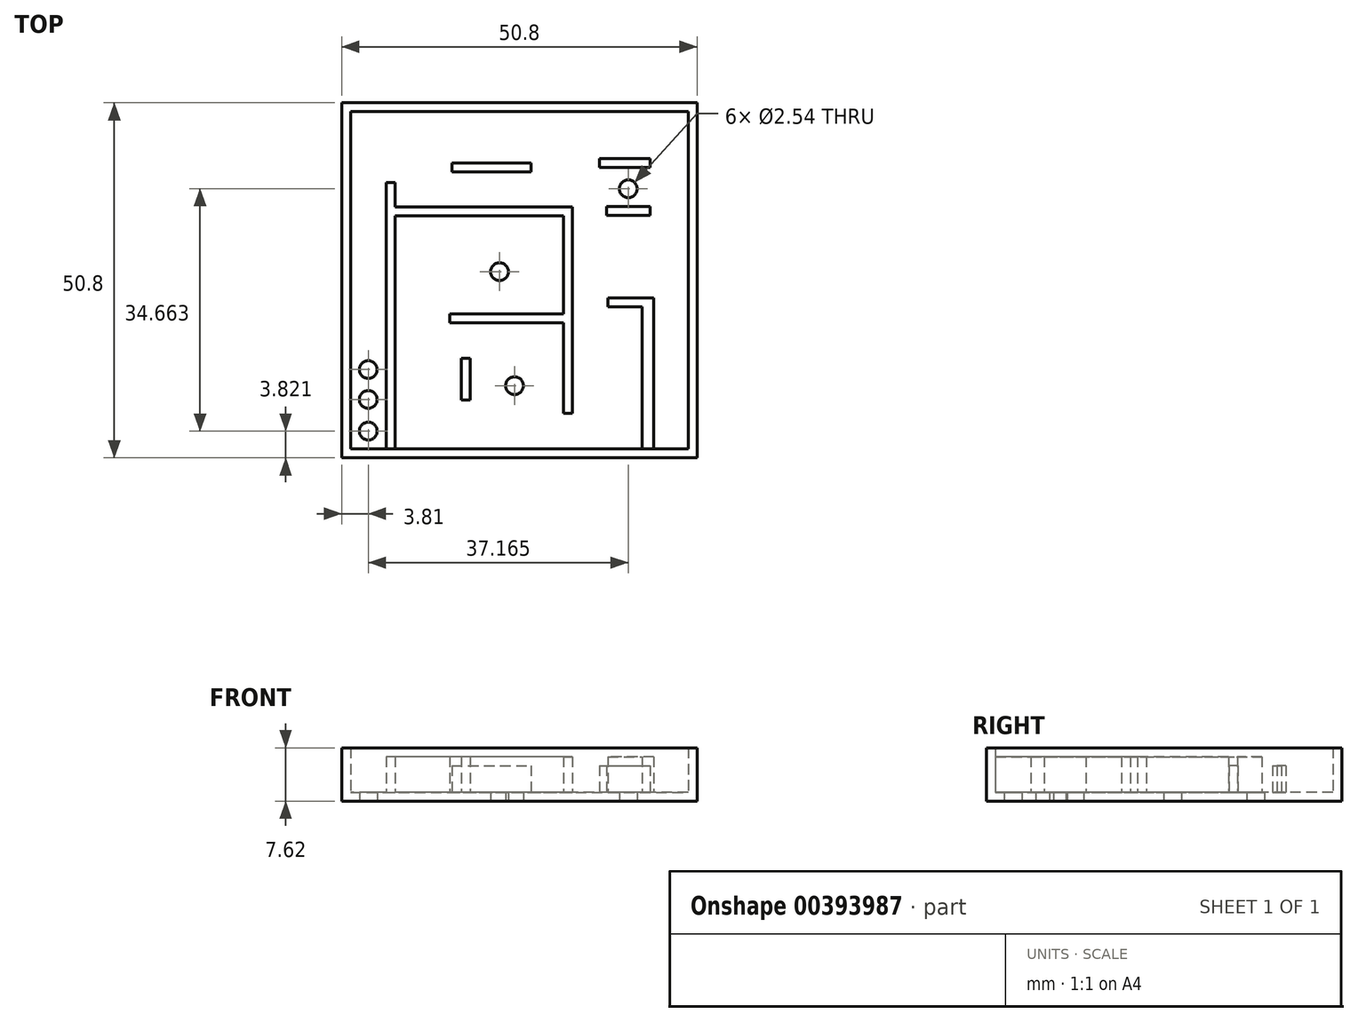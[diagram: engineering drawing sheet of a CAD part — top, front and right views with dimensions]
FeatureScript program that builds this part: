
annotation { "Feature Type Name" : "Feature", "Feature Type Description" : "" }
export const myFeature = defineFeature(function(context is Context, id is Id, definition is map)
    precondition{}
    {
        {
            var Q0;
            Q0=qCreatedBy(makeId("Top.planeOp"),FACE);
            var sketch = newSketch(context, id + "F0", { "sketchPlane" : qUnion([Q0])});
            skLineSegment(sketch, "E0", {"start": v(0, 0) * mm, "end": v(0, 50.8) * mm});
            skLineSegment(sketch, "E1", {"start": v(0, 50.8) * mm, "end": v(50.8, 50.8) * mm});
            skLineSegment(sketch, "E2", {"start": v(50.8, 50.8) * mm, "end": v(50.8, 0) * mm});
            skLineSegment(sketch, "E3", {"start": v(50.8, 0) * mm, "end": v(0, 0) * mm});
            skSolve(sketch);
        }
        {
            var Q0;
            Q0 = qSketchRegion(id + "F0", true);
            extrude(context, id + "F1", {"entities" : qUnion([Q0]), "depth" : 7.62 * mm});
        }
        {
            var Q0;
            Q0=makeQuery(id+"F1.opExtrude","CAP_FACE",FACE,{"disambiguationData":[OSD([sQuery(id+"F0.wireOp",EDGE,"E0"),sQuery(id+"F0.wireOp",EDGE,"E1"),sQuery(id+"F0.wireOp",EDGE,"E2"),sQuery(id+"F0.wireOp",EDGE,"E3")])],"isStart":false});
            shell(context, id + "F2", {"entities" : qUnion([Q0]), "thickness" : 1.27 * mm});
        }
        {
            var Q0;
            Q0=makeQuery(id+"F2.opShell","OFFSET_FACE",FACE,{"disambiguationData":[OSD([sQuery(id+"F0.wireOp",EDGE,"E0"),sQuery(id+"F0.wireOp",EDGE,"E1"),sQuery(id+"F0.wireOp",EDGE,"E2"),sQuery(id+"F0.wireOp",EDGE,"E3")])]});
            var sketch = newSketch(context, id + "F3", { "sketchPlane" : qUnion([Q0])});
            skLineSegment(sketch, "E4", {"start": v(6.35, 1.27) * mm, "end": v(6.35, 39.38) * mm});
            skLineSegment(sketch, "E5", {"start": v(6.35, 39.38) * mm, "end": v(7.62, 39.38) * mm});
            skLineSegment(sketch, "E6", {"start": v(7.62, 39.38) * mm, "end": v(7.62, 1.27) * mm});
            skLineSegment(sketch, "E7", {"start": v(7.62, 1.27) * mm, "end": v(6.35, 1.27) * mm});
            skLineSegment(sketch, "E8", {"start": v(7.62, 35.88) * mm, "end": v(31.69, 35.88) * mm});
            skLineSegment(sketch, "E9", {"start": v(31.69, 35.88) * mm, "end": v(31.69, 34.61) * mm});
            skLineSegment(sketch, "E10", {"start": v(31.69, 34.61) * mm, "end": v(7.62, 34.61) * mm});
            skLineSegment(sketch, "E11", {"start": v(7.62, 34.61) * mm, "end": v(7.62, 35.88) * mm});
            skLineSegment(sketch, "E12", {"start": v(31.69, 34.61) * mm, "end": v(31.69, 6.35) * mm});
            skLineSegment(sketch, "E13", {"start": v(31.69, 6.35) * mm, "end": v(32.96, 6.35) * mm});
            skLineSegment(sketch, "E14", {"start": v(32.96, 6.35) * mm, "end": v(32.96, 35.88) * mm});
            skLineSegment(sketch, "E15", {"start": v(32.96, 35.88) * mm, "end": v(31.69, 35.88) * mm});
            skLineSegment(sketch, "E16", {"start": v(38.04, 22.84) * mm, "end": v(38.04, 21.57) * mm});
            skLineSegment(sketch, "E17", {"start": v(38.04, 21.57) * mm, "end": v(44.62, 21.57) * mm});
            skLineSegment(sketch, "E18", {"start": v(44.62, 21.57) * mm, "end": v(44.62, 22.84) * mm});
            skLineSegment(sketch, "E19", {"start": v(44.62, 22.84) * mm, "end": v(38.04, 22.84) * mm});
            skLineSegment(sketch, "E20", {"start": v(44.62, 21.57) * mm, "end": v(44.62, 1.27) * mm});
            skLineSegment(sketch, "E21", {"start": v(44.62, 1.27) * mm, "end": v(49.53, 1.27) * mm});
            skLineSegment(sketch, "E22", {"start": v(49.53, 1.27) * mm, "end": v(49.53, 22.84) * mm});
            skLineSegment(sketch, "E23", {"start": v(42.98, 21.57) * mm, "end": v(42.98, 1.27) * mm});
            skLineSegment(sketch, "E24", {"start": v(31.69, 20.56) * mm, "end": v(15.45, 20.56) * mm});
            skLineSegment(sketch, "E25", {"start": v(15.45, 20.56) * mm, "end": v(15.45, 19.29) * mm});
            skLineSegment(sketch, "E26", {"start": v(15.45, 19.29) * mm, "end": v(31.69, 19.29) * mm});
            skCircle(sketch, "E27", {"center": v(3.3, 5.26) * mm, "radius": 1.27 * mm});
            skLineSegment(sketch, "E28", {"start": v(17.09, 14.2) * mm, "end": v(17.09, 8.28) * mm});
            skLineSegment(sketch, "E29", {"start": v(17.09, 8.28) * mm, "end": v(18.36, 8.28) * mm});
            skLineSegment(sketch, "E30", {"start": v(18.36, 8.28) * mm, "end": v(18.36, 14.2) * mm});
            skLineSegment(sketch, "E31", {"start": v(18.36, 14.2) * mm, "end": v(17.09, 14.2) * mm});
            skSolve(sketch);
        }
        {
            var Q0;
            Q0=makeQuery(id+"F3.imprint","IMPRINT",FACE,{"disambiguationData":[TD([[makeQuery(id+"F3.imprint","IMPRINT",EDGE,{"derivedFrom":sQuery(id+"F3.wireOp",EDGE,"E4")}),-1.0]])]});
            var Q1;
            {var subQ0=sQuery(id+"F3.wireOp",EDGE,"E24");Q1=makeQuery(id+"F3.imprint","IMPRINT",FACE,{"disambiguationData":[TD([[makeQuery(id+"F3.imprint","IMPRINT",EDGE,{"derivedFrom":subQ0}),1.0]])]});}
            var Q2;
            Q2=makeQuery(id+"F3.imprint","IMPRINT",FACE,{"disambiguationData":[TD([[makeQuery(id+"F3.imprint","IMPRINT",EDGE,{"derivedFrom":sQuery(id+"F3.wireOp",EDGE,"E28")}),1.0]])]});
            var Q3;
            {var subQ3=sQuery(id+"F3.wireOp",EDGE,"E9");Q3=makeQuery(id+"F3.imprint","IMPRINT",FACE,{"disambiguationData":[TD([[makeQuery(id+"F3.imprint","IMPRINT",EDGE,{"derivedFrom":subQ3}),1.0]])]});}
            var Q4;
            Q4=makeQuery(id+"F3.imprint","IMPRINT",FACE,{"disambiguationData":[TD([[makeQuery(id+"F3.imprint","IMPRINT",EDGE,{"derivedFrom":sQuery(id+"F3.wireOp",EDGE,"E8")}),-1.0]])]});
            var Q5;
            {var subQ3=sQuery(id+"F3.wireOp",EDGE,"E16");Q5=makeQuery(id+"F3.imprint","IMPRINT",FACE,{"disambiguationData":[TD([[makeQuery(id+"F3.imprint","IMPRINT",EDGE,{"derivedFrom":subQ3}),1.0]])]});}
            var Q6;
            {var subQ0=sQuery(id+"F3.wireOp",EDGE,"E20");Q6=makeQuery(id+"F3.imprint","IMPRINT",FACE,{"disambiguationData":[TD([[makeQuery(id+"F3.imprint","IMPRINT",EDGE,{"derivedFrom":subQ0}),-1.0]])]});}
            extrude(context, id + "F4", {"entities" : qUnion([Q0, Q1, Q2, Q3, Q4, Q5, Q6]), "operationType" : NewBodyOperationType.ADD, "depth" : 5.08 * mm});
        }
        {
            var Q0;
            Q0=qCreatedBy(makeId("Top.planeOp"),FACE);
            var sketch = newSketch(context, id + "F5", { "sketchPlane" : qUnion([Q0])});
            skLineSegment(sketch, "E32.bottom", {"start": v(36.83, 42.78) * mm, "end": v(44.1, 42.78) * mm});
            skLineSegment(sketch, "E32.top", {"start": v(36.83, 41.5) * mm, "end": v(44.1, 41.5) * mm});
            skLineSegment(sketch, "E32.left", {"start": v(36.83, 42.78) * mm, "end": v(36.83, 41.5) * mm});
            skLineSegment(sketch, "E32.right", {"start": v(44.1, 42.78) * mm, "end": v(44.1, 41.5) * mm});
            skLineSegment(sketch, "E33.bottom", {"start": v(37.85, 35.94) * mm, "end": v(44.1, 35.94) * mm});
            skLineSegment(sketch, "E33.top", {"start": v(37.85, 34.67) * mm, "end": v(44.1, 34.67) * mm});
            skLineSegment(sketch, "E33.left", {"start": v(37.85, 35.94) * mm, "end": v(37.85, 34.67) * mm});
            skLineSegment(sketch, "E33.right", {"start": v(44.1, 35.94) * mm, "end": v(44.1, 34.67) * mm});
            skSolve(sketch);
        }
        {
            var Q0;
            Q0 = qSketchRegion(id + "F5", true);
            extrude(context, id + "F6", {"entities" : qUnion([Q0]), "operationType" : NewBodyOperationType.ADD, "depth" : 5.08 * mm});
        }
        {
            var Q0;
            Q0=qCreatedBy(makeId("Top.planeOp"),FACE);
            var sketch = newSketch(context, id + "F7", { "sketchPlane" : qUnion([Q0])});
            skCircle(sketch, "E34", {"center": v(3.81, 3.82) * mm, "radius": 1.27 * mm});
            skCircle(sketch, "E35", {"center": v(3.81, 8.34) * mm, "radius": 1.27 * mm});
            skCircle(sketch, "E36", {"center": v(3.81, 12.62) * mm, "radius": 1.27 * mm});
            skCircle(sketch, "E37", {"center": v(40.98, 38.48) * mm, "radius": 1.27 * mm});
            skCircle(sketch, "E38", {"center": v(22.57, 26.62) * mm, "radius": 1.27 * mm});
            skSolve(sketch);
        }
        {
            var Q0;
            Q0 = qSketchRegion(id + "F7", true);
            extrude(context, id + "F8", {"entities" : qUnion([Q0]), "operationType" : NewBodyOperationType.REMOVE, "depth" : 203.2 * mm});
        }
        {
            var Q0;
            Q0=qCreatedBy(makeId("Top.planeOp"),FACE);
            var sketch = newSketch(context, id + "F9", { "sketchPlane" : qUnion([Q0])});
            skLineSegment(sketch, "E39", {"start": v(15.77, 42.15) * mm, "end": v(27.06, 42.15) * mm});
            skLineSegment(sketch, "E40", {"start": v(27.06, 42.15) * mm, "end": v(27.06, 40.88) * mm});
            skLineSegment(sketch, "E41", {"start": v(27.06, 40.88) * mm, "end": v(15.77, 40.88) * mm});
            skLineSegment(sketch, "E42", {"start": v(15.77, 40.88) * mm, "end": v(15.77, 42.15) * mm});
            skSolve(sketch);
        }
        {
            var Q0;
            Q0 = qSketchRegion(id + "F9", true);
            extrude(context, id + "F10", {"entities" : qUnion([Q0]), "operationType" : NewBodyOperationType.ADD, "depth" : 5.08 * mm});
        }
        {
            var Q0;
            Q0=qCreatedBy(makeId("Top.planeOp"),FACE);
            var sketch = newSketch(context, id + "F11", { "sketchPlane" : qUnion([Q0])});
            skCircle(sketch, "E43", {"center": v(24.72, 10.32) * mm, "radius": 1.27 * mm});
            skSolve(sketch);
        }
        {
            var Q0;
            Q0 = qSketchRegion(id + "F11", true);
            extrude(context, id + "F12", {"entities" : qUnion([Q0]), "operationType" : NewBodyOperationType.REMOVE, "depth" : 203.2 * mm});
        }
    });
